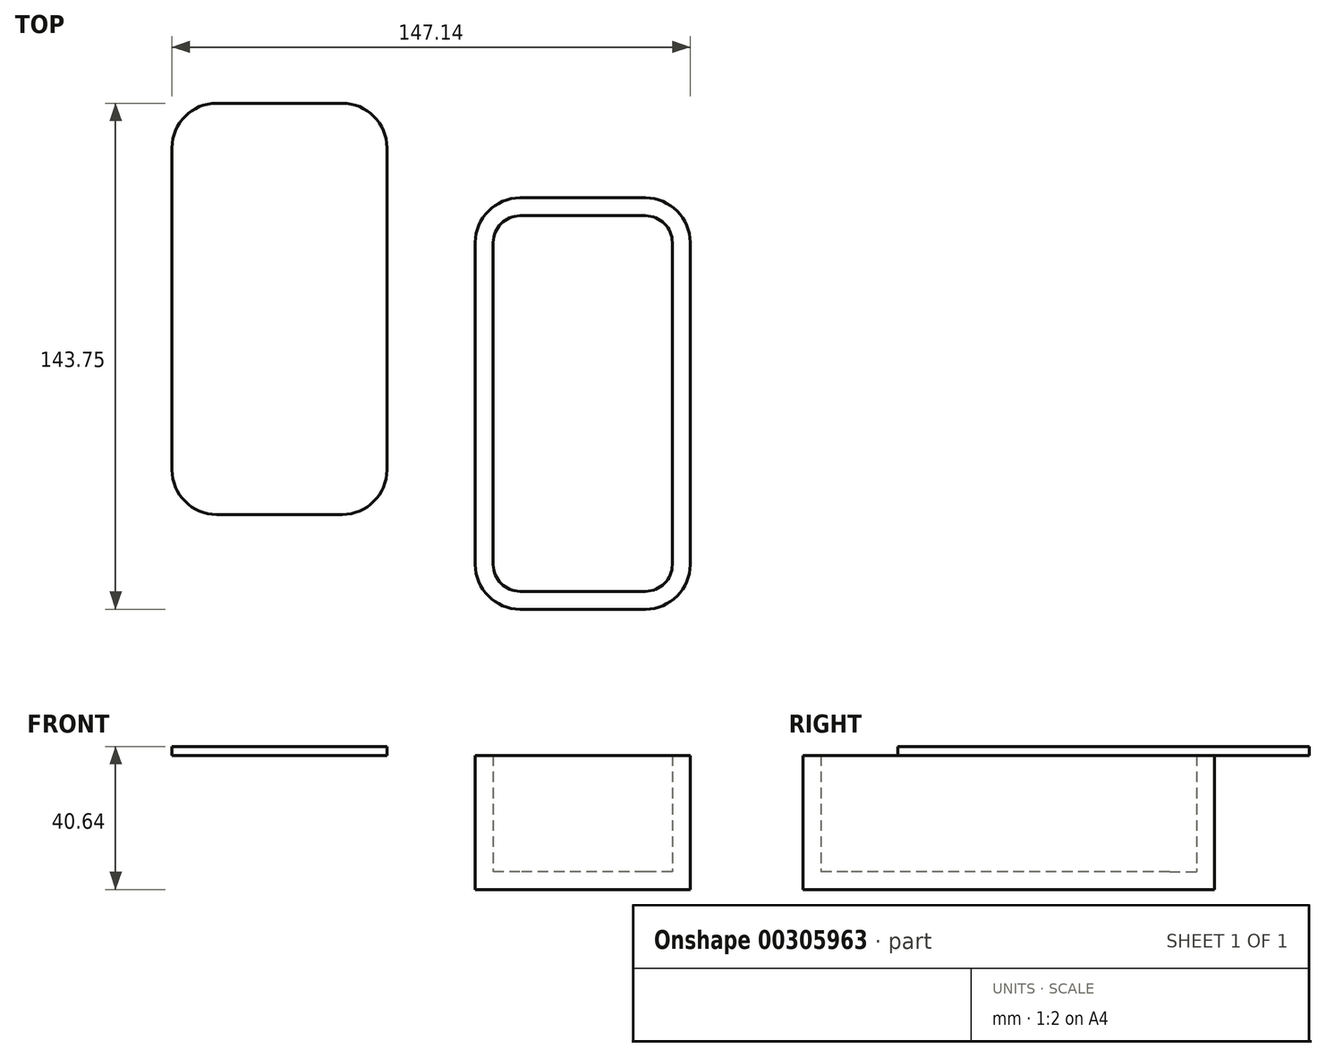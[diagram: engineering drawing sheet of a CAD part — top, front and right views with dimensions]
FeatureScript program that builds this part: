
annotation { "Feature Type Name" : "Feature", "Feature Type Description" : "" }
export const myFeature = defineFeature(function(context is Context, id is Id, definition is map)
    precondition{}
    {
        {
            var Q0;
            Q0=qCreatedBy(makeId("Top.planeOp"),FACE);
            var sketch = newSketch(context, id + "F0", { "sketchPlane" : qUnion([Q0])});
            skLineSegment(sketch, "E0.bottom", {"start": v(17.8, 58.42) * mm, "end": v(-17.8, 58.42) * mm});
            skLineSegment(sketch, "E0.top", {"start": v(17.8, -58.42) * mm, "end": v(-17.8, -58.42) * mm});
            skLineSegment(sketch, "E0.left", {"start": v(30.5, 45.72) * mm, "end": v(30.5, -45.72) * mm});
            skLineSegment(sketch, "E0.right", {"start": v(-30.5, 45.72) * mm, "end": v(-30.5, -45.72) * mm});
            skPoint(sketch, "E0.middle", {"position": v(0, 0) * mm});
            skPoint(sketch, "E1.visualSharp", {"position": v(-30.5, 58.42) * mm});
            skArc(sketch, "E1.filletArc", {"start": v(-17.8, 58.42) * mm, "mid": v(-26.79, 54.7) * mm, "end": v(-30.5, 45.72) * mm});
            skPoint(sketch, "E2.visualSharp", {"position": v(30.5, 58.42) * mm});
            skArc(sketch, "E2.filletArc", {"start": v(30.5, 45.72) * mm, "mid": v(26.79, 54.7) * mm, "end": v(17.8, 58.42) * mm});
            skPoint(sketch, "E3.visualSharp", {"position": v(30.5, -58.42) * mm});
            skArc(sketch, "E3.filletArc", {"start": v(17.8, -58.42) * mm, "mid": v(26.79, -54.7) * mm, "end": v(30.5, -45.72) * mm});
            skPoint(sketch, "E4.visualSharp", {"position": v(-30.5, -58.42) * mm});
            skArc(sketch, "E4.filletArc", {"start": v(-30.5, -45.72) * mm, "mid": v(-26.79, -54.7) * mm, "end": v(-17.8, -58.42) * mm});
            skSolve(sketch);
        }
        {
            var Q0;
            Q0 = qSketchRegion(id + "F0", true);
            extrude(context, id + "F1", {"entities" : qUnion([Q0]), "depth" : 38.1 * mm});
        }
        {
            var Q0;
            Q0=makeQuery(id+"F1.opExtrude","CAP_FACE",FACE,{"disambiguationData":[OSD([sQuery(id+"F0.wireOp",EDGE,"E0.bottom"),sQuery(id+"F0.wireOp",EDGE,"E0.top"),sQuery(id+"F0.wireOp",EDGE,"E0.left"),sQuery(id+"F0.wireOp",EDGE,"E0.right"),sQuery(id+"F0.wireOp",EDGE,"E1.filletArc"),sQuery(id+"F0.wireOp",EDGE,"E2.filletArc"),sQuery(id+"F0.wireOp",EDGE,"E3.filletArc"),sQuery(id+"F0.wireOp",EDGE,"E4.filletArc")])],"isStart":false});
            shell(context, id + "F2", {"entities" : qUnion([Q0]), "thickness" : 5.08 * mm});
        }
        {
            var Q0;
            Q0=makeQuery(id+"F1.opExtrude","CAP_FACE",FACE,{"disambiguationData":[OSD([sQuery(id+"F0.wireOp",EDGE,"E0.bottom"),sQuery(id+"F0.wireOp",EDGE,"E0.top"),sQuery(id+"F0.wireOp",EDGE,"E0.left"),sQuery(id+"F0.wireOp",EDGE,"E0.right"),sQuery(id+"F0.wireOp",EDGE,"E1.filletArc"),sQuery(id+"F0.wireOp",EDGE,"E2.filletArc"),sQuery(id+"F0.wireOp",EDGE,"E3.filletArc"),sQuery(id+"F0.wireOp",EDGE,"E4.filletArc")])],"isStart":false});
            var sketch = newSketch(context, id + "F3", { "sketchPlane" : qUnion([Q0])});
            skLineSegment(sketch, "E5.bottom", {"start": v(-68.32, 85.33) * mm, "end": v(-103.93, 85.33) * mm});
            skLineSegment(sketch, "E5.top", {"start": v(-68.32, -31.52) * mm, "end": v(-103.93, -31.52) * mm});
            skLineSegment(sketch, "E5.left", {"start": v(-55.62, 72.63) * mm, "end": v(-55.62, -18.82) * mm});
            skLineSegment(sketch, "E5.right", {"start": v(-116.63, 72.63) * mm, "end": v(-116.63, -18.82) * mm});
            skPoint(sketch, "E5.middle", {"position": v(-86.13, 26.9) * mm});
            skPoint(sketch, "E6.visualSharp", {"position": v(-116.63, 85.33) * mm});
            skArc(sketch, "E6.filletArc", {"start": v(-103.93, 85.33) * mm, "mid": v(-112.91, 81.61) * mm, "end": v(-116.63, 72.63) * mm});
            skPoint(sketch, "E7.visualSharp", {"position": v(-55.62, 85.33) * mm});
            skArc(sketch, "E7.filletArc", {"start": v(-55.62, 72.63) * mm, "mid": v(-59.34, 81.61) * mm, "end": v(-68.32, 85.33) * mm});
            skPoint(sketch, "E8.visualSharp", {"position": v(-55.62, -31.52) * mm});
            skArc(sketch, "E8.filletArc", {"start": v(-68.32, -31.52) * mm, "mid": v(-59.34, -27.8) * mm, "end": v(-55.62, -18.82) * mm});
            skPoint(sketch, "E9.visualSharp", {"position": v(-116.63, -31.52) * mm});
            skArc(sketch, "E9.filletArc", {"start": v(-116.63, -18.82) * mm, "mid": v(-112.91, -27.8) * mm, "end": v(-103.93, -31.52) * mm});
            skSolve(sketch);
        }
        {
            var Q0;
            Q0=makeQuery(id+"F3.imprint","IMPRINT",FACE,{"disambiguationData":[TD([[makeQuery(id+"F3.imprint","IMPRINT",EDGE,{"derivedFrom":sQuery(id+"F3.wireOp",EDGE,"E5.bottom")}),1.0]])]});
            extrude(context, id + "F4", {"entities" : qUnion([Q0]), "depth" : 2.54 * mm});
        }
    });
